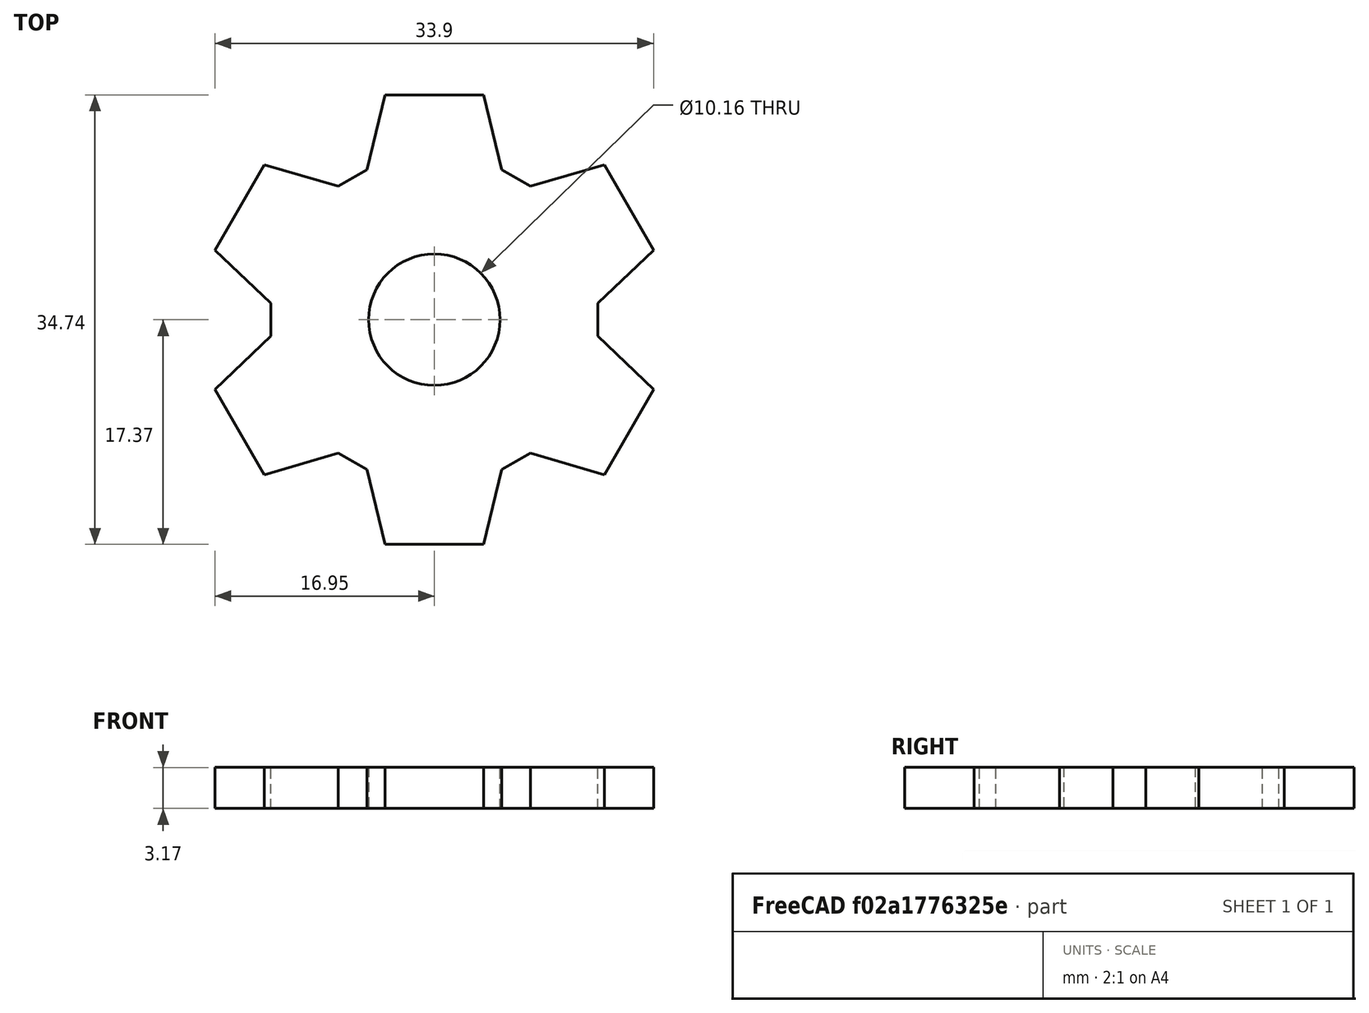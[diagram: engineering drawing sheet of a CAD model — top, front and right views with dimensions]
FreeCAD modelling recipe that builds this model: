
FCSTD DOCUMENT  (FreeCAD 0.20R26651 (Git))
Label: Mechanical_Template
License: All rights reserved
LicenseURL: http://en.wikipedia.org/wiki/All_rights_reserved
objects: TechDraw::DrawViewDimension×3, TechDraw::DrawViewDimExtent×2, Sketcher::SketchObject×1, PartDesign::Pad×1, PartDesign::Body×1, TechDraw::DrawSVGTemplate×1, TechDraw::DrawProjGroupItem×1, TechDraw::DrawProjGroup×1, TechDraw::DrawPage×1
note: 4 computed .brp shape members not serialized (recipe doc carries the construction recipe); baked Part::Feature solids carry a one-line shape summary decoded from their .brp

FEATURE [Sketcher::SketchObject] Sketch
  FullyConstrained = true
  MapMode = 5
  Support = -> [XY_Plane]
  sketch-geometry (27):
    g0: Circle CenterX=0 CenterY=0 CenterZ=0 NormalX=0 NormalY=0 NormalZ=1 AngleXU=0 Radius=12.7
    g1: LineSegment StartX=-5.21832 StartY=11.5784 StartZ=0 EndX=-3.81 EndY=17.367 EndZ=0
    g2: LineSegment StartX=-3.81 StartY=17.367 StartZ=0 EndX=3.81 EndY=17.367 EndZ=0
    g3: LineSegment StartX=3.81 StartY=17.367 StartZ=0 EndX=5.21832 EndY=11.5784 EndZ=0
    g4: LineSegment StartX=5.21832 StartY=11.5784 StartZ=0 EndX=7.41802 EndY=10.3084 EndZ=0
    g5: LineSegment StartX=7.41802 StartY=10.3084 StartZ=0 EndX=13.1353 EndY=11.9831 EndZ=0
    g6: LineSegment StartX=13.1353 StartY=11.9831 StartZ=0 EndX=16.9453 EndY=5.38394 EndZ=0
    g7: LineSegment StartX=16.9453 StartY=5.38394 StartZ=0 EndX=12.6363 EndY=1.27 EndZ=0
    g8: LineSegment StartX=12.6363 StartY=1.27 StartZ=0 EndX=12.6363 EndY=-1.27 EndZ=0
    g9: LineSegment StartX=12.6363 StartY=-1.27 StartZ=0 EndX=16.9453 EndY=-5.38394 EndZ=0
    g10: LineSegment StartX=16.9453 StartY=-5.38394 StartZ=0 EndX=13.1353 EndY=-11.9831 EndZ=0
    g11: LineSegment StartX=13.1353 StartY=-11.9831 StartZ=0 EndX=7.41802 EndY=-10.3084 EndZ=0
    g12: LineSegment StartX=7.41802 StartY=-10.3084 StartZ=0 EndX=5.21832 EndY=-11.5784 EndZ=0
    g13: LineSegment StartX=5.21832 StartY=-11.5784 StartZ=0 EndX=3.81 EndY=-17.367 EndZ=0
    g14: LineSegment StartX=3.81 StartY=-17.367 StartZ=0 EndX=-3.81 EndY=-17.367 EndZ=0
    g15: LineSegment StartX=-3.81 StartY=-17.367 StartZ=0 EndX=-5.21832 EndY=-11.5784 EndZ=0
    g16: LineSegment StartX=-5.21832 StartY=-11.5784 StartZ=0 EndX=-7.41802 EndY=-10.3084 EndZ=0
    g17: LineSegment StartX=-7.41802 StartY=-10.3084 StartZ=0 EndX=-13.1353 EndY=-11.9831 EndZ=0
    g18: LineSegment StartX=-13.1353 StartY=-11.9831 StartZ=0 EndX=-16.9453 EndY=-5.38394 EndZ=0
    g19: LineSegment StartX=-16.9453 StartY=-5.38394 StartZ=0 EndX=-12.6363 EndY=-1.27 EndZ=0
    g20: LineSegment StartX=-12.6363 StartY=-1.27 StartZ=0 EndX=-12.6363 EndY=1.27 EndZ=0
    g21: LineSegment StartX=-12.6363 StartY=1.27 StartZ=0 EndX=-16.9453 EndY=5.38394 EndZ=0
    g22: LineSegment StartX=-16.9453 StartY=5.38394 StartZ=0 EndX=-13.1353 EndY=11.9831 EndZ=0
    g23: LineSegment StartX=-13.1353 StartY=11.9831 StartZ=0 EndX=-7.41802 EndY=10.3084 EndZ=0
    g24: LineSegment StartX=-7.41802 StartY=10.3084 StartZ=0 EndX=-5.21832 EndY=11.5784 EndZ=0
    g25: Circle CenterX=-1.5687e-12 CenterY=0 CenterZ=0 NormalX=0 NormalY=0 NormalZ=1 AngleXU=0 Radius=17.78
    g26: Circle CenterX=0 CenterY=0 CenterZ=0 NormalX=0 NormalY=0 NormalZ=1 AngleXU=0 Radius=5.08
  constraints (79):
    c: Coincident(g0,g-1)
    c: PointOnObject(g1,g0)
    c: Coincident(g2,g1)
    c: Coincident(g3,g2)
    c: PointOnObject(g3,g0)
    c: Horizontal(g2)
    c: Coincident(g3,g4)
    c: PointOnObject(g4,g0)
    c: Coincident(g4,g5)
    c: Coincident(g5,g6)
    c: Coincident(g6,g7)
    c: PointOnObject(g7,g0)
    c: Coincident(g7,g8)
    c: PointOnObject(g8,g0)
    c: Coincident(g8,g9)
    c: Coincident(g9,g10)
    c: Coincident(g10,g11)
    c: PointOnObject(g11,g0)
    c: Coincident(g11,g12)
    c: PointOnObject(g12,g0)
    c: Coincident(g12,g13)
    c: Coincident(g13,g14)
    c: Horizontal(g14)
    c: Coincident(g14,g15)
    c: PointOnObject(g15,g0)
    c: Coincident(g15,g16)
    c: PointOnObject(g16,g0)
    c: Coincident(g16,g17)
    c: Coincident(g17,g18)
    c: Coincident(g18,g19)
    c: PointOnObject(g19,g0)
    c: Coincident(g19,g20)
    c: PointOnObject(g20,g0)
    c: Coincident(g20,g21)
    c: Coincident(g21,g22)
    c: Coincident(g22,g23)
    c: PointOnObject(g23,g0)
    c: Coincident(g23,g24)
    c: Coincident(g24,g1)
    c: Equal(g24,g4)
    c: Equal(g4,g8)
    c: Equal(g8,g12)
    c: Equal(g12,g16)
    c: Equal(g16,g20)
    c: Equal(g22,g2)
    c: Equal(g2,g6)
    c: Equal(g6,g10)
    c: Equal(g10,g14)
    c: Equal(g14,g18)
    c: Equal(g21,g23)
    c: Equal(g23,g1)
    c: Equal(g1,g3)
    c: Equal(g3,g5)
    c: Equal(g5,g7)
    c: Equal(g7,g9)
    c: Equal(g9,g11)
    c: Equal(g11,g13)
    c: Equal(g13,g15)
    c: Equal(g15,g17)
    c: Equal(g17,g19)
    c: Distance(g24) = 2.54
    c: Distance(g2) = 7.62
    c: PointOnObject(g25,g-1)
    c: PointOnObject(g5,g25)
    c: PointOnObject(g6,g25)
    c: PointOnObject(g9,g25)
    c: PointOnObject(g10,g25)
    c: PointOnObject(g13,g25)
    c: PointOnObject(g14,g25)
    c: PointOnObject(g17,g25)
    c: PointOnObject(g18,g25)
    c: PointOnObject(g21,g25)
    c: PointOnObject(g22,g25)
    c: PointOnObject(g1,g25)
    c: PointOnObject(g2,g25)
    c: Diameter(g25) = 35.56
    c: Diameter(g0) = 25.4
    c: Coincident(g26,g-1)
    c: Diameter(g26) = 10.16
FEATURE [PartDesign::Pad] Pad
  Direction = (0,0,1)
  Length = 3.175
  Length2 = 100.076
  Profile = -> Sketch
  ReferenceAxis = -> Sketch [N_Axis]
  Type = 0
FEATURE [PartDesign::Body] Body  label="Mechanical Template Body"
  Group = -> [Sketch,Pad]
  Origin = -> Origin
  Tip = -> Pad
FEATURE [TechDraw::DrawSVGTemplate] Template
  EditableTexts = Designed_by_Name=Design by Matthew; Drawing_number=e130a642; FC-Date=Dec 2021; FC-SC=1:1; FC-SH=1 of 1; FC-Title=Mechanical Subteam Patch; Subtitle=Tidal Force Robotics; Weight=0.01
  Height = 210
  Orientation = 1
  Width = 297
FEATURE [TechDraw::DrawProjGroupItem] ProjItem  label="Front"
  CoarseView = false
  Direction = (0,0,1)
  Focus = 100
  HardHidden = false
  IsoCount = 0
  IsoHidden = false
  IsoVisible = false
  LockPosition = true
  Perspective = false
  Rotation = 0
  RotationVector = (1,0,0)
  ScaleType = 2
  SeamHidden = false
  SeamVisible = true
  SmoothHidden = false
  SmoothVisible = true
  Source = -> [Body]
  Type = 0
  X = 0
  XDirection = (1,0,0)
  Y = 0
FEATURE [TechDraw::DrawProjGroup] ProjGroup
  Anchor = -> ProjItem
  AutoDistribute = true
  LockPosition = false
  ProjectionType = 0
  Rotation = 0
  ScaleType = 0
  Source = -> [Body]
  Views = -> [ProjItem]
  X = 144.22
  Y = 119.552
  spacingX = 14.986
  spacingY = 14.986
FEATURE [TechDraw::DrawViewDimExtent] DimExtent
  Arbitrary = false
  ArbitraryTolerances = false
  CosmeticTags = a0b890dd-8765-4fee-9e34-aeeeac7e49b4 | e671eb48-c5cb-4831-bf0c-24cd2488b197
  DirExtent = 1
  EqualTolerance = true
  FormatSpec = %.3f
  FormatSpecOverTolerance = %+.3f
  FormatSpecUnderTolerance = %+.3f
  Inverted = false
  LockPosition = false
  MeasureType = 1
  OverTolerance = 0
  References2D = -> [ProjItem]
  Rotation = 0
  ScaleType = 0
  Source = -> [ProjItem]
  TheoreticalExact = false
  Type = 2
  UnderTolerance = 0
  X = 29.3091
  Y = 1.88416
FEATURE [TechDraw::DrawViewDimExtent] DimExtent001
  Arbitrary = false
  ArbitraryTolerances = false
  CosmeticTags = d0842a71-5413-4fad-bf8b-849824d42d1e | 3237898e-1e8d-4b71-998b-0cab7fef200c
  DirExtent = 0
  EqualTolerance = true
  FormatSpec = %.3f
  FormatSpecOverTolerance = %+.3f
  FormatSpecUnderTolerance = %+.3f
  Inverted = false
  LockPosition = false
  MeasureType = 1
  OverTolerance = 0
  References2D = -> [ProjItem]
  Rotation = 0
  ScaleType = 0
  Source = -> [ProjItem]
  TheoreticalExact = false
  Type = 1
  UnderTolerance = 0
  X = 0.418702
  Y = -28.7857
FEATURE [TechDraw::DrawViewDimension] Dimension
  Arbitrary = false
  ArbitraryTolerances = false
  EqualTolerance = true
  FormatSpec = ⌀%.3f
  FormatSpecOverTolerance = %+.3f
  FormatSpecUnderTolerance = %+.3f
  Inverted = false
  LockPosition = false
  MeasureType = 1
  OverTolerance = 0
  References2D = -> [ProjItem]
  Rotation = 0
  ScaleType = 0
  TheoreticalExact = false
  Type = 5
  UnderTolerance = 0
  X = -28.7857
  Y = 4.39637
FEATURE [TechDraw::DrawViewDimension] Dimension001
  Arbitrary = false
  ArbitraryTolerances = false
  EqualTolerance = true
  FormatSpec = %.3f
  FormatSpecOverTolerance = %+.3f
  FormatSpecUnderTolerance = %+.3f
  Inverted = false
  LockPosition = false
  MeasureType = 1
  OverTolerance = 0
  References2D = -> [ProjItem]
  Rotation = 0
  ScaleType = 0
  TheoreticalExact = false
  Type = 0
  UnderTolerance = 0
  X = -24.3624
  Y = 27.0313
FEATURE [TechDraw::DrawViewDimension] Dimension002
  Arbitrary = false
  ArbitraryTolerances = false
  EqualTolerance = true
  FormatSpec = %.3f
  FormatSpecOverTolerance = %+.3f
  FormatSpecUnderTolerance = %+.3f
  Inverted = false
  LockPosition = false
  MeasureType = 1
  OverTolerance = 0
  References2D = -> [ProjItem]
  Rotation = 0
  ScaleType = 0
  TheoreticalExact = false
  Type = 0
  UnderTolerance = 0
  X = -16.2701
  Y = 27.9734
FEATURE [TechDraw::DrawPage] Page
  KeepUpdated = true
  NextBalloonIndex = 1
  ProjectionType = 0
  Template = -> Template
  Views = -> [ProjGroup,DimExtent,DimExtent001,Dimension,Dimension001,Dimension002]
